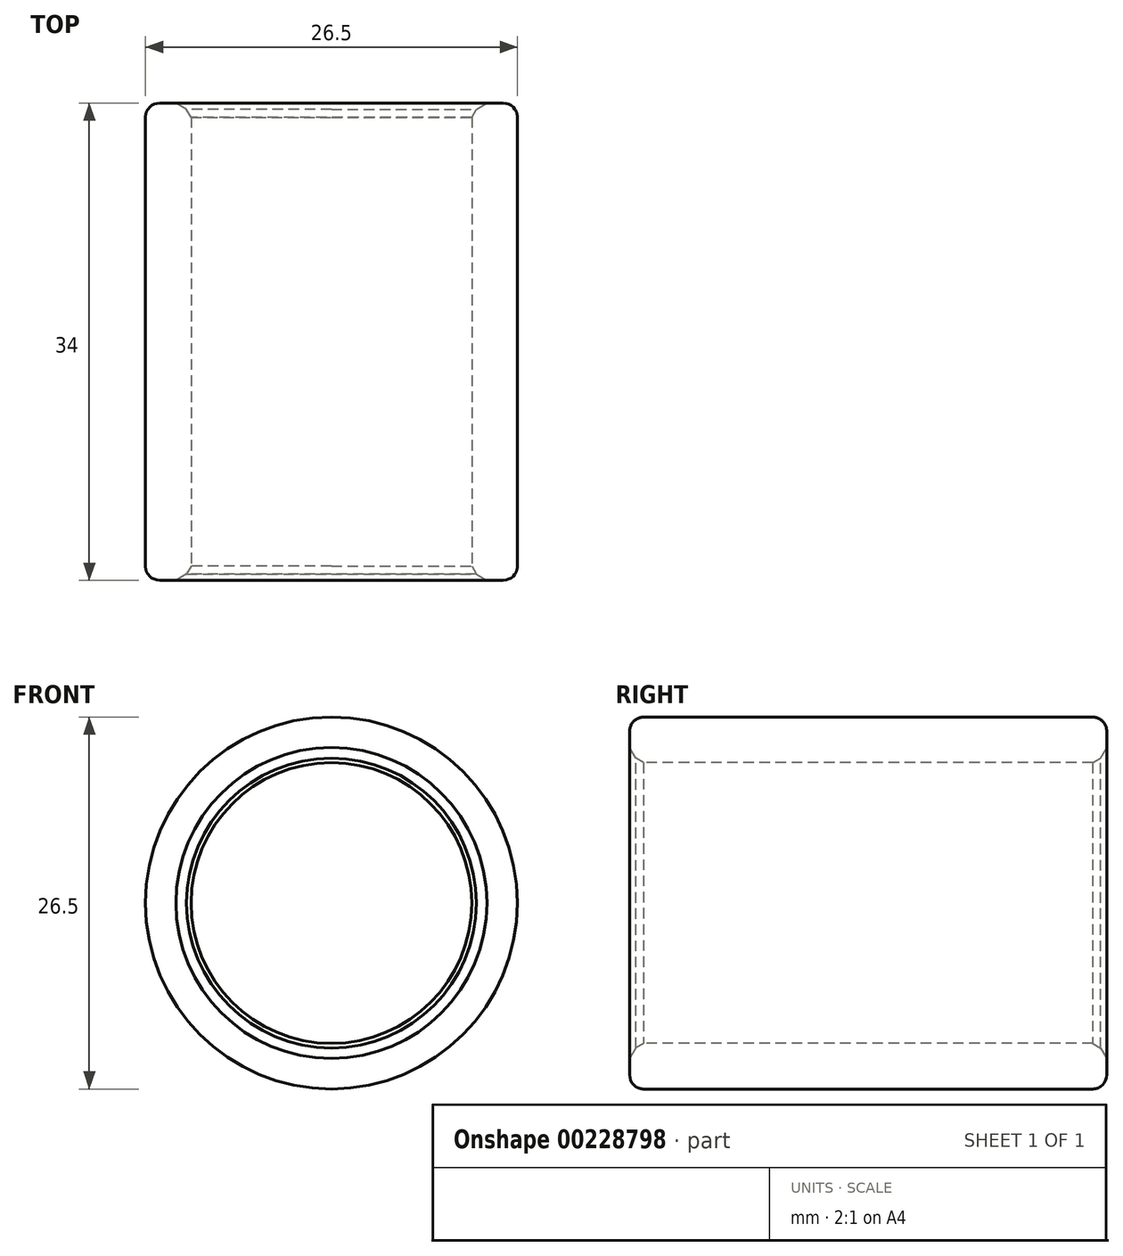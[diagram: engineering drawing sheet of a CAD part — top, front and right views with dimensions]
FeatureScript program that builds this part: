
annotation { "Feature Type Name" : "Feature", "Feature Type Description" : "" }
export const myFeature = defineFeature(function(context is Context, id is Id, definition is map)
    precondition{}
    {
        {
            var Q0;
            Q0=qCreatedBy(makeId("Right.planeOp"),FACE);
            var sketch = newSketch(context, id + "F0", { "sketchPlane" : qUnion([Q0])});
            skLineSegment(sketch, "E0.bottom", {"start": v(-17, 13.25) * mm, "end": v(17, 13.25) * mm});
            skLineSegment(sketch, "E0.top", {"start": v(-17, 10) * mm, "end": v(17, 10) * mm});
            skLineSegment(sketch, "E0.left", {"start": v(-17, 13.25) * mm, "end": v(-17, 10) * mm});
            skLineSegment(sketch, "E0.right", {"start": v(17, 13.25) * mm, "end": v(17, 10) * mm});
            skPoint(sketch, "E0.middle", {"position": v(0, 11.63) * mm});
            skLineSegment(sketch, "E1", {"start": v(-3.47, 0) * mm, "end": v(3.5, 0) * mm});
            skSolve(sketch);
        }
        {
            var Q0;
            Q0=makeQuery(id+"F0.imprint","IMPRINT",FACE,{"disambiguationData":[TD([[makeQuery(id+"F0.imprint","IMPRINT",EDGE,{"derivedFrom":sQuery(id+"F0.wireOp",EDGE,"E0.bottom")}),-1.0]])]});
            var Q1;
            Q1=sQuery(id+"F0.wireOp",EDGE,"E1");
            revolve(context, id + "F1", {"entities" : qUnion([Q0]), "axis" : qUnion([Q1]), "revolveType" : RevolveType.FULL});
        }
        {
            var Q0;
            Q0=makeQuery(id+"F1.opRevolve","SWEPT_EDGE",EDGE,{"disambiguationData":[OSD([sQuery(id+"F0.wireOp",EDGE,"E0.top"),sQuery(id+"F0.wireOp",EDGE,"E0.left")])]});
            var Q1;
            Q1=makeQuery(id+"F1.opRevolve","SWEPT_EDGE",EDGE,{"disambiguationData":[OSD([sQuery(id+"F0.wireOp",EDGE,"E0.top"),sQuery(id+"F0.wireOp",EDGE,"E0.right")])]});
            chamfer(context, id + "F2", {"entities" : qUnion([Q0, Q1]), "chamferType" : ChamferType.OFFSET_ANGLE, "width" : 1 * mm, "oppositeDirection" : false, "angle" : 30 * degree, "tangentPropagation" : true});
        }
        {
            var Q0;
            {var subQ0=sQuery(id+"F0.wireOp",EDGE,"E0.left");Q0=makeQuery(id+"F2.opChamfer","BLEND_EDGE",EDGE,{"blendedFrom":[makeQuery(id+"F1.opRevolve","SWEPT_EDGE",EDGE,{"disambiguationData":[OSD([sQuery(id+"F0.wireOp",EDGE,"E0.top"),subQ0])]}),makeQuery(id+"F1.opRevolve","SWEPT_FACE",FACE,{"disambiguationData":[OSD([subQ0])]})],"blendedInto":[makeQuery(id+"F1.opRevolve","SWEPT_FACE",FACE,{"disambiguationData":[OSD([subQ0])]})]});}
            var Q1;
            {var subQ0=sQuery(id+"F0.wireOp",EDGE,"E0.right");Q1=makeQuery(id+"F2.opChamfer","BLEND_EDGE",EDGE,{"blendedFrom":[makeQuery(id+"F1.opRevolve","SWEPT_EDGE",EDGE,{"disambiguationData":[OSD([sQuery(id+"F0.wireOp",EDGE,"E0.top"),subQ0])]}),makeQuery(id+"F1.opRevolve","SWEPT_FACE",FACE,{"disambiguationData":[OSD([subQ0])]})],"blendedInto":[makeQuery(id+"F1.opRevolve","SWEPT_FACE",FACE,{"disambiguationData":[OSD([subQ0])]})]});}
            chamfer(context, id + "F3", {"entities" : qUnion([Q0, Q1]), "chamferType" : ChamferType.TWO_OFFSETS, "width1" : .5 * mm, "oppositeDirection" : false, "width2" : .5 * mm, "tangentPropagation" : true});
        }
        {
            var Q0;
            Q0=makeQuery(id+"F1.opRevolve","SWEPT_EDGE",EDGE,{"disambiguationData":[OSD([sQuery(id+"F0.wireOp",EDGE,"E0.bottom"),sQuery(id+"F0.wireOp",EDGE,"E0.right")])]});
            var Q1;
            Q1=makeQuery(id+"F1.opRevolve","SWEPT_EDGE",EDGE,{"disambiguationData":[OSD([sQuery(id+"F0.wireOp",EDGE,"E0.bottom"),sQuery(id+"F0.wireOp",EDGE,"E0.left")])]});
            fillet(context, id + "F4", {"entities" : qUnion([Q0, Q1]), "radius" : 1 * mm, "tangentPropagation" : true, "allowEdgeOverflow" : false});
        }
    });
